# Revit family: Drinking_Fountain-Haws_Corporation-Wall_Mounted_1117ln
name_source: partatom
category: Plumbing Fixtures
units: mm (PartAtom-declared; Revit-internal decimal feet)

## family parameters
Always vertical = Yes
Cut with Voids When Loaded = No
Host = Wall
OmniClass Number = 23.65.70.14.11
OmniClass Title = Drinking Fountains/Coolers
Part Type = Normal
Room Calculation Point = No
Round Connector Dimension = Use Radius
Shared = Yes

## types (1)
- Not a Type - Load Type Catalog!
    Apparent Load = 0 VA
    Assembly Code = D2010810
    BIMobject category = Taps & Mixers
    BIMobject category code = sanitary-taps-mixers
    BIMobject main category = Sanitary
    BIMobject main category code = sanitary
    BP32 Panel = Yes
    Back Panel = Metal - Haws Corporation - Satin Stainless Steel
    Basin Height = 4 1/4"
    Basin Width = 12"
    Beep Level = 0"
    Bottle Filler 1920 = Yes
    Bowl = Metal - Haws Corporation - Satin Stainless Steel
    Brand url = https://www.hawsco.com
    CW Connection = Yes
    CWFU = 1
    Cost = $0
    Cost Note = For Cost information please visit the Resource tab in the Product Page URL
    Current = 1 A
    Description = "Hi-Lo" drinking fountain and bottle filler uses patented stainless steel, push-button activated valve assemblies allowing for front access stream adjustment as well as cartridge and strainer access.
    Design country = United States
    Edition number = 1
    Electrical Connection Note = Electrical connection is only required for products that contain touchless sensors
    Flow = 0.00 GPM
    HW Connection = No
    HWFU = 0
    Keynote = 15410.A1
    Manufacturer = Haws Corporation 1455 Kleppe Lane Sparks, NV 89431
    Manufacturer country = United States
    Manufacturer name = Haws Corporation
    Masterformat 2014 Code = 22 47 13
    Masterformat 2014 Description = Drinking Fountains
    Material main = Stainless steel
    Model = 1117LN-1920-BP32
    NBS Reference Code = 35-65-70-25
    NBS Reference Description = Drinking Fountain Systems
    Nominal height = 13"
    Nominal width = 28"
    Nr = 3
    Nr 2 = 3
    Number of Poles = 1
    OmniClass Code = 23-31 31 00
    OmniClass Description = Drinking Fountains
    Power Factor = 1
    Product Page URL = https://www.hawsco.com
    Product SKU = haws-1117LN
    Product data url = https://www.bimobject.com
    Product family = Drinking Fountains/Coolers
    Product group = Wall Mounted Drinking Fountains
    QR code = http://bimobject.com
    Sanitary Radius = 5/8"
    Sensor 1 = Yes
    Sensor 2 = Yes
    Series = The Haws 1117 adjustable barrier free Hi-Lo drinking fountain
    Supply Radius = 1/4"
    Supply_No = 3
    Trim = Metal - Haws Corporation - Satin Stainless Steel
    Tubing = Metal - Haws Corporation - Copper Poly
    Type Comments = "Hi-Lo" drinking fountain with antimicrobial protection* uses a patented push-button valve assembly
    UNSPSC Code = 301815
    URL = http://www.hawsco.com
    Uniclass 1.4 Code = L7213
    Uniclass 1.4 Description = Fountains
    Uniclass 2.0 Code = SS-35-65-70-25
    Uniclass 2.0 Description = Drinking Fountain Systems
    Uniclass 2015 Code = Pr_40_20_87_24
    Uniclass 2015 Name = Drinking fountains
    Vent Connection = Yes
    Voltage = 0 V
    WFU = 1
    Waste Connection = Yes
    Weight Net (Kg) = 69
    z_Masking = No

## geometry (parser evidence)
native form markers: Sweep x15
no freeform markers — native parametric forms only
